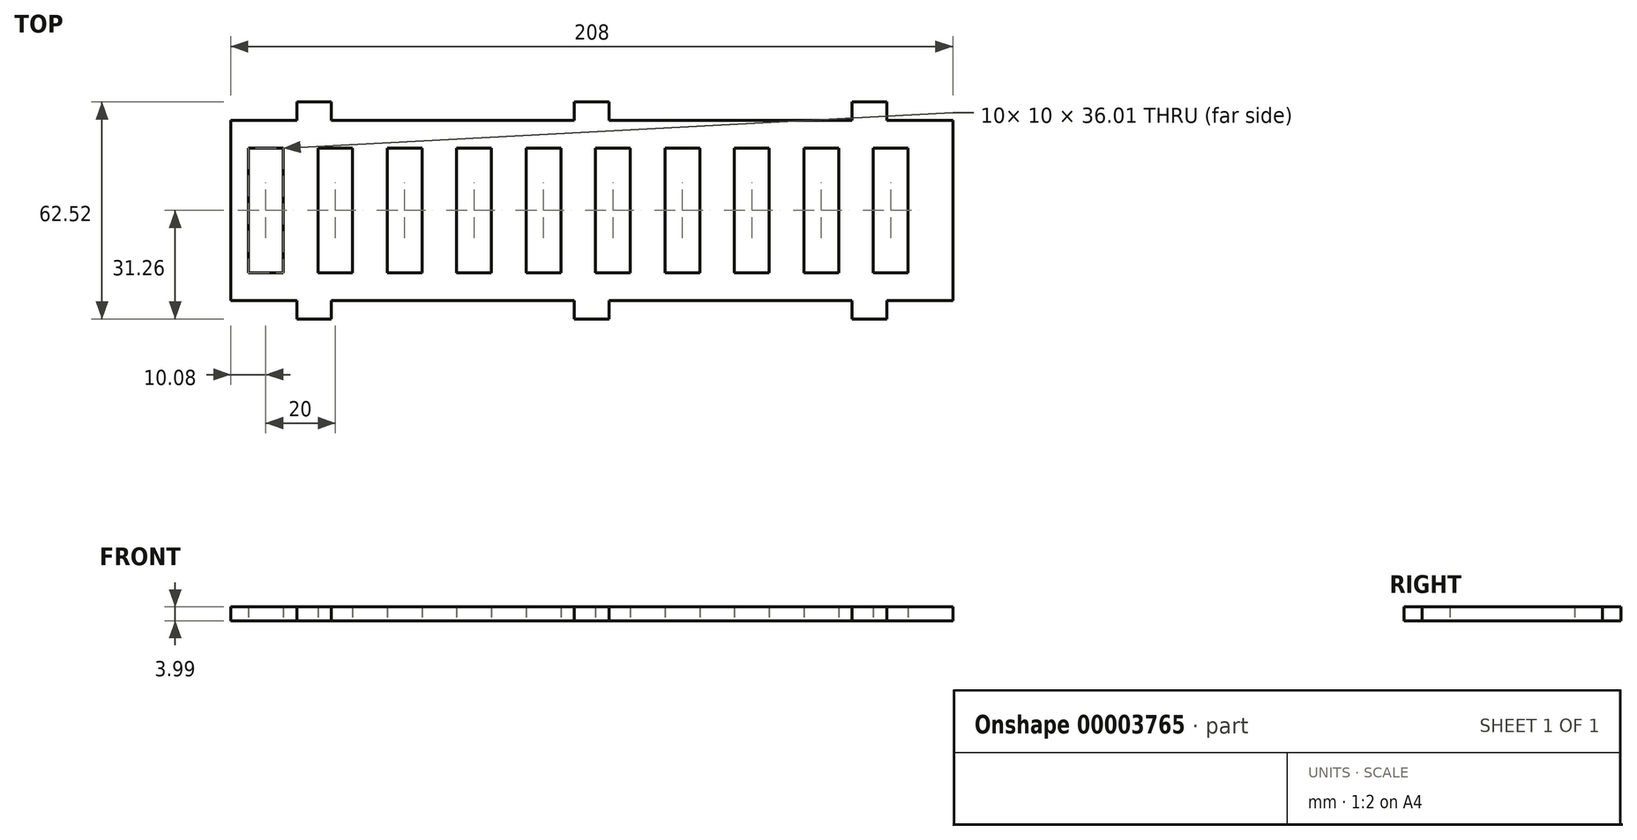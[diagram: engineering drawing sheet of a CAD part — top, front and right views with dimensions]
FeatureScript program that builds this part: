
annotation { "Feature Type Name" : "Feature", "Feature Type Description" : "" }
export const myFeature = defineFeature(function(context is Context, id is Id, definition is map)
    precondition{}
    {
        {
            var Q0;
            Q0=qCreatedBy(makeId("Top.planeOp"),FACE);
            var sketch = newSketch(context, id + "F0", { "sketchPlane" : qUnion([Q0])});
            skLineSegment(sketch, "E0.rect.bottom", {"start": v(-104, 26) * mm, "end": v(-85, 26) * mm});
            skLineSegment(sketch, "E0.rect.top", {"start": v(-104, -26) * mm, "end": v(-85, -26) * mm});
            skLineSegment(sketch, "E0.rect.left", {"start": v(-104, 26) * mm, "end": v(-104, -26) * mm});
            skLineSegment(sketch, "E0.rect.right", {"start": v(104, 26) * mm, "end": v(104, -26) * mm});
            skPoint(sketch, "E0.rect.middle", {"position": v(0, 0) * mm});
            skLineSegment(sketch, "E1.rect.bottom", {"start": v(-5, 31.26) * mm, "end": v(5, 31.26) * mm});
            skLineSegment(sketch, "E1.rect.left", {"start": v(-5, 31.26) * mm, "end": v(-5, 26) * mm});
            skLineSegment(sketch, "E1.rect.right", {"start": v(5, 31.26) * mm, "end": v(5, 26) * mm});
            skPoint(sketch, "E1.rect.middle", {"position": v(0, 26) * mm});
            skPoint(sketch, "E1.rect.top.start.orphan", {"position": v(-5, 20.74) * mm});
            skPoint(sketch, "E2.orphan", {"position": v(5, 20.74) * mm});
            skLineSegment(sketch, "E3.trimOffspring", {"start": v(5, 26) * mm, "end": v(75, 26) * mm});
            skLineSegment(sketch, "E4.1.0.0", {"start": v(75, 31.26) * mm, "end": v(75, 26) * mm});
            skLineSegment(sketch, "E4.1.0.1", {"start": v(75, 31.26) * mm, "end": v(85, 31.26) * mm});
            skLineSegment(sketch, "E4.1.0.2", {"start": v(85, 31.26) * mm, "end": v(85, 26) * mm});
            skLineSegment(sketch, "E4.direction1", {"start": v(-5, 26) * mm, "end": v(75, 26) * mm, "construction": true});
            skLineSegment(sketch, "E5.1.0.0", {"start": v(-85, 31.26) * mm, "end": v(-75, 31.26) * mm});
            skLineSegment(sketch, "E5.1.0.1", {"start": v(-85, 31.26) * mm, "end": v(-85, 26) * mm});
            skLineSegment(sketch, "E5.1.0.2", {"start": v(-75, 31.26) * mm, "end": v(-75, 26) * mm});
            skLineSegment(sketch, "E5.direction1", {"start": v(-5, 31.26) * mm, "end": v(-85, 31.26) * mm, "construction": true});
            skLineSegment(sketch, "E6.trimOffspring", {"start": v(-75, 26) * mm, "end": v(-5, 26) * mm});
            skLineSegment(sketch, "E7.trimOffspring", {"start": v(85, 26) * mm, "end": v(104, 26) * mm});
            skLineSegment(sketch, "E8", {"start": v(0, 0) * mm, "end": v(-104, 0) * mm, "construction": true});
            skLineSegment(sketch, "E9.0.MirrorCS", {"start": v(-85, -31.26) * mm, "end": v(-85, -26) * mm});
            skLineSegment(sketch, "E10.0.MirrorCS", {"start": v(-85, -31.26) * mm, "end": v(-75, -31.26) * mm});
            skLineSegment(sketch, "E11.0.MirrorCS", {"start": v(-75, -31.26) * mm, "end": v(-75, -26) * mm});
            skLineSegment(sketch, "E12.0.MirrorCS", {"start": v(-5, -31.26) * mm, "end": v(-5, -26) * mm});
            skLineSegment(sketch, "E13.0.MirrorCS", {"start": v(-5, -31.26) * mm, "end": v(5, -31.26) * mm});
            skLineSegment(sketch, "E14.0.MirrorCS", {"start": v(5, -31.26) * mm, "end": v(5, -26) * mm});
            skLineSegment(sketch, "E15.0.MirrorCS", {"start": v(75, -31.26) * mm, "end": v(75, -26) * mm});
            skLineSegment(sketch, "E16.0.MirrorCS", {"start": v(75, -31.26) * mm, "end": v(85, -31.26) * mm});
            skLineSegment(sketch, "E17.0.MirrorCS", {"start": v(85, -31.26) * mm, "end": v(85, -26) * mm});
            skLineSegment(sketch, "E18.trimOffspring", {"start": v(-75, -26) * mm, "end": v(-5, -26) * mm});
            skLineSegment(sketch, "E19.trimOffspring", {"start": v(5, -26) * mm, "end": v(75, -26) * mm});
            skLineSegment(sketch, "E20.trimOffspring", {"start": v(85, -26) * mm, "end": v(104, -26) * mm});
            skLineSegment(sketch, "E21.rect.bottom", {"start": v(-98.92, 18) * mm, "end": v(-88.92, 18) * mm});
            skLineSegment(sketch, "E21.rect.top", {"start": v(-98.92, -18) * mm, "end": v(-88.92, -18) * mm});
            skLineSegment(sketch, "E21.rect.left", {"start": v(-98.92, 18) * mm, "end": v(-98.92, -18) * mm});
            skLineSegment(sketch, "E21.rect.right", {"start": v(-88.92, 18) * mm, "end": v(-88.92, -18) * mm});
            skPoint(sketch, "E21.rect.middle", {"position": v(-93.92, 0) * mm});
            skLineSegment(sketch, "E22.1.0.0", {"start": v(-78.92, 18) * mm, "end": v(-78.92, -18) * mm});
            skLineSegment(sketch, "E22.1.0.1", {"start": v(-78.92, 18) * mm, "end": v(-68.92, 18) * mm});
            skLineSegment(sketch, "E22.1.0.2", {"start": v(-68.92, 18) * mm, "end": v(-68.92, -18) * mm});
            skLineSegment(sketch, "E22.1.0.3", {"start": v(-78.92, -18) * mm, "end": v(-68.92, -18) * mm});
            skLineSegment(sketch, "E22.2.0.0", {"start": v(-58.92, 18) * mm, "end": v(-58.92, -18) * mm});
            skLineSegment(sketch, "E22.2.0.1", {"start": v(-58.92, 18) * mm, "end": v(-48.92, 18) * mm});
            skLineSegment(sketch, "E22.2.0.2", {"start": v(-48.92, 18) * mm, "end": v(-48.92, -18) * mm});
            skLineSegment(sketch, "E22.2.0.3", {"start": v(-58.92, -18) * mm, "end": v(-48.92, -18) * mm});
            skLineSegment(sketch, "E22.3.0.0", {"start": v(-38.92, 18) * mm, "end": v(-38.92, -18) * mm});
            skLineSegment(sketch, "E22.3.0.1", {"start": v(-38.92, 18) * mm, "end": v(-28.92, 18) * mm});
            skLineSegment(sketch, "E22.3.0.2", {"start": v(-28.92, 18) * mm, "end": v(-28.92, -18) * mm});
            skLineSegment(sketch, "E22.3.0.3", {"start": v(-38.92, -18) * mm, "end": v(-28.92, -18) * mm});
            skLineSegment(sketch, "E22.4.0.0", {"start": v(-18.92, 18) * mm, "end": v(-18.92, -18) * mm});
            skLineSegment(sketch, "E22.4.0.1", {"start": v(-18.92, 18) * mm, "end": v(-8.92, 18) * mm});
            skLineSegment(sketch, "E22.4.0.2", {"start": v(-8.92, 18) * mm, "end": v(-8.92, -18) * mm});
            skLineSegment(sketch, "E22.4.0.3", {"start": v(-18.92, -18) * mm, "end": v(-8.92, -18) * mm});
            skLineSegment(sketch, "E22.5.0.0", {"start": v(1.08, 18) * mm, "end": v(1.08, -18) * mm});
            skLineSegment(sketch, "E22.5.0.1", {"start": v(1.08, 18) * mm, "end": v(11.08, 18) * mm});
            skLineSegment(sketch, "E22.5.0.2", {"start": v(11.08, 18) * mm, "end": v(11.08, -18) * mm});
            skLineSegment(sketch, "E22.5.0.3", {"start": v(1.08, -18) * mm, "end": v(11.08, -18) * mm});
            skLineSegment(sketch, "E22.6.0.0", {"start": v(21.08, 18) * mm, "end": v(21.08, -18) * mm});
            skLineSegment(sketch, "E22.6.0.1", {"start": v(21.08, 18) * mm, "end": v(31.08, 18) * mm});
            skLineSegment(sketch, "E22.6.0.2", {"start": v(31.08, 18) * mm, "end": v(31.08, -18) * mm});
            skLineSegment(sketch, "E22.6.0.3", {"start": v(21.08, -18) * mm, "end": v(31.08, -18) * mm});
            skLineSegment(sketch, "E22.7.0.0", {"start": v(41.08, 18) * mm, "end": v(41.08, -18) * mm});
            skLineSegment(sketch, "E22.7.0.1", {"start": v(41.08, 18) * mm, "end": v(51.08, 18) * mm});
            skLineSegment(sketch, "E22.7.0.2", {"start": v(51.08, 18) * mm, "end": v(51.08, -18) * mm});
            skLineSegment(sketch, "E22.7.0.3", {"start": v(41.08, -18) * mm, "end": v(51.08, -18) * mm});
            skLineSegment(sketch, "E22.direction1", {"start": v(-98.92, -18) * mm, "end": v(-78.92, -18) * mm, "construction": true});
            skLineSegment(sketch, "E23.0.8.0", {"start": v(61.08, 18) * mm, "end": v(61.08, -18) * mm});
            skLineSegment(sketch, "E23.3.8.0", {"start": v(61.08, 18) * mm, "end": v(71.08, 18) * mm});
            skLineSegment(sketch, "E23.6.8.0", {"start": v(71.08, 18) * mm, "end": v(71.08, -18) * mm});
            skLineSegment(sketch, "E23.9.8.0", {"start": v(61.08, -18) * mm, "end": v(71.08, -18) * mm});
            skLineSegment(sketch, "E23.0.9.0", {"start": v(81.08, 18) * mm, "end": v(81.08, -18) * mm});
            skLineSegment(sketch, "E23.3.9.0", {"start": v(81.08, 18) * mm, "end": v(91.08, 18) * mm});
            skLineSegment(sketch, "E23.6.9.0", {"start": v(91.08, 18) * mm, "end": v(91.08, -18) * mm});
            skLineSegment(sketch, "E23.9.9.0", {"start": v(81.08, -18) * mm, "end": v(91.08, -18) * mm});
            skSolve(sketch);
        }
        {
            var Q0;
            Q0=makeQuery(id+"F0.imprint","IMPRINT",FACE,{"disambiguationData":[TD([[makeQuery(id+"F0.imprint","IMPRINT",EDGE,{"derivedFrom":sQuery(id+"F0.wireOp",EDGE,"E0.rect.bottom")}),-1.0]])]});
            extrude(context, id + "F1", {"entities" : qUnion([Q0]), "depth" : 4 * mm});
        }
    });
